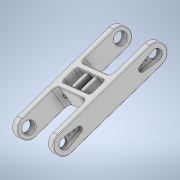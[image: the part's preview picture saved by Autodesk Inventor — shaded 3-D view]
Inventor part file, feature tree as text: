
AUTODESK INVENTOR PART (.ipt)
format: ipt  version: 2020.3 (Build 243373000, 373)  size: 493,568 bytes
history: native  units: mm
features: fillet x12, sketch x7, extrude x6, hole x3
ambient origin geometry x8: Origin, YZ Plane, XZ Plane, XY Plane, X Axis, Y Axis, Z Axis, Center Point
bodies: Solid1 (feature_tree)
feature tree (28):
  extrude  "Extrusion1"  Depth=34.0mm
  sketch  "Sketch2"  dims[d11=20.0mm d12=15.0mm d13=0.0mm d14=3.0mm d15=6.0mm d16=4.0mm d19=6.0mm d20=0.0mm]
  extrude  "Extrusion2"  Depth=15.0mm TaperAngle=0.0deg
  fillet  "Fillet1"  Radius=3.0mm
  fillet  "Fillet2"  Radius=6.0mm
  fillet  "Fillet3"  Radius=4.0mm
  fillet  "Fillet4"  Radius=6.0mm
  sketch  "Sketch5"  dims[d30=35.0mm d31=35.0mm]
  extrude  "Extrusion4"  Depth=35.0mm
  extrude  "Extrusion5"  Depth=12.1mm
  hole  "Hole7"  [1 undecoded]
  extrude  "Extrusion6"  Depth=1.0mm TaperAngle=0.0deg
  extrude  "Extrusion7"  Depth=10.0mm
  hole  "Hole5"  [1 undecoded]
  fillet  "Fillet13"  Radius=3.0mm
  fillet  "Fillet11"  Radius=0.5mm
  fillet  "Fillet9"  Radius=2.0mm
  fillet  "Fillet15"  Radius=0.2mm
  fillet  "Fillet12"  Radius=3.5mm
  hole  "Hole6"  [1 undecoded]
  fillet  "Fillet14"  Radius=0.5mm
  fillet  "Fillet16"  Radius=0.5mm
  fillet  "Fillet17"  Radius=0.3mm
  sketch  "Sketch1"  dims[d2=6.0mm d8=34.0mm]
  sketch  "Sketch6"  dims[d53=3.7mm d54=12.1mm]
  sketch  "Sketch12"  dims[d61=4.0mm d62=0.0mm d63=3.5mm d64=0.0mm]
  sketch  "Sketch13"  dims[d68=1.0mm d69=0.0mm d70=1.0mm d71=0.0mm]
  sketch  "Sketch14"  dims[d72=1.0mm d76=12.1mm d89=7.2mm d97=3.0mm d98=3.0mm d99=6.0mm d100=4.0mm d101=2.0mm d102=90.0deg d103=5.0mm d104=20.594885mm d105=0.5mm d107=2.0mm d108=0.2mm d109=3.5mm d110=8.7mm d111=6.0mm d112=4.0mm d113=2.0mm d114=90.0deg d115=5.0mm d116=20.594885mm d117=0.5mm d118=0.5mm d119=0.5mm d120=0.3mm d121=2.0mm d122=2.0mm d123=2.0mm d124=1.0mm d125=6.0mm d126=4.0mm d127=2.0mm d128=90.0deg d129=10.0mm d130=20.594885mm]
note: 3 required parameter values undecoded (feature->parameter linkage not recoverable at this tier; creation-order binding heuristic only, values carry confidence <= 0.55)
